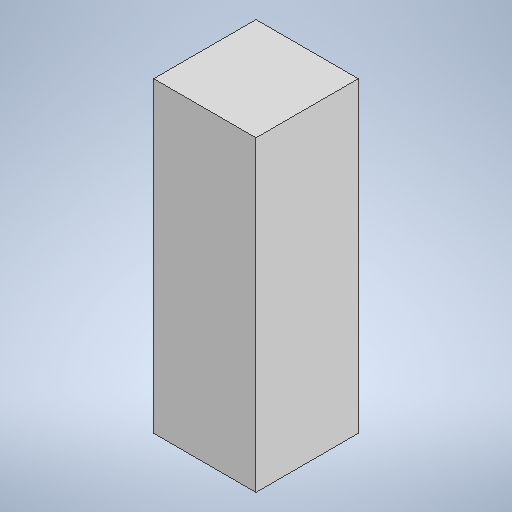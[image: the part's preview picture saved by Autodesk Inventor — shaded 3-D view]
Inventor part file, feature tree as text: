
AUTODESK INVENTOR PART (.ipt)
format: ipt  version: 2025 (Build 290162010, 162A)  size: 208,384 bytes
history: native  units: mm
features: extrude x1, sketch x1
ambient origin geometry x8: Origin, YZ Plane, XZ Plane, XY Plane, X Axis, Y Axis, Z Axis, Center Point
bodies: Solid1 (feature_tree)
feature tree (2):
  extrude  "Extrusion1"  Depth=400.0mm
  sketch  "Sketch1"  dims[d0=400.0mm d1=400.0mm d2=1200.0mm d3=0.0mm]
